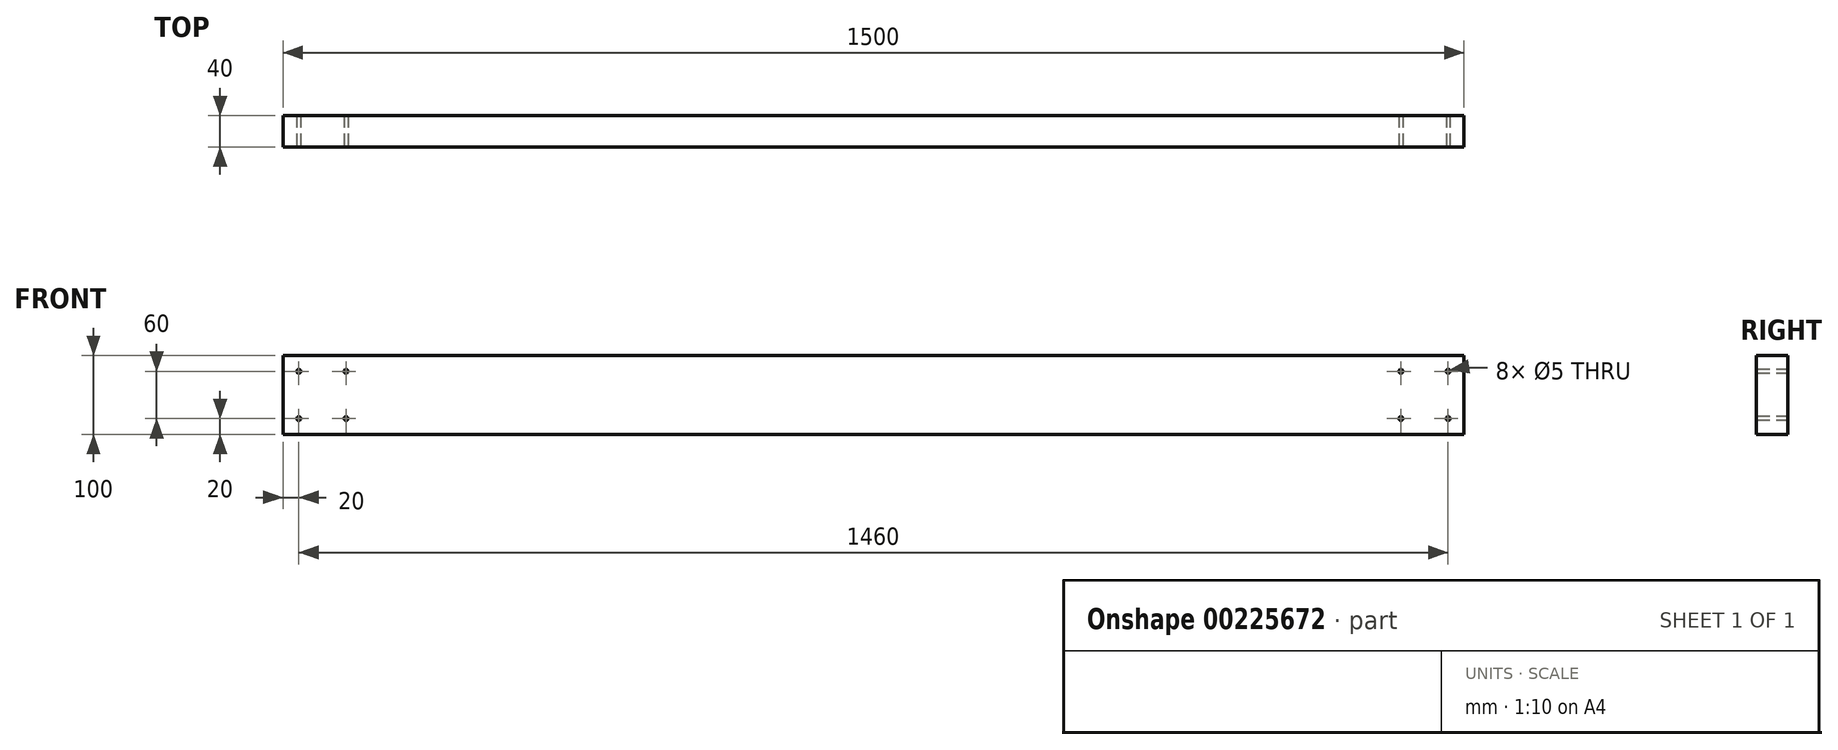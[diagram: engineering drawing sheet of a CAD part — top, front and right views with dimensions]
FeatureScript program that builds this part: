
annotation { "Feature Type Name" : "Feature", "Feature Type Description" : "" }
export const myFeature = defineFeature(function(context is Context, id is Id, definition is map)
    precondition{}
    {
        {
            var Q0;
            Q0=qCreatedBy(makeId("Front.planeOp"),FACE);
            var sketch = newSketch(context, id + "F0", { "sketchPlane" : qUnion([Q0])});
            skLineSegment(sketch, "E0.bottom", {"start": v(-750, 50) * mm, "end": v(750, 50) * mm});
            skLineSegment(sketch, "E0.top", {"start": v(-750, -50) * mm, "end": v(750, -50) * mm});
            skLineSegment(sketch, "E0.left", {"start": v(-750, 50) * mm, "end": v(-750, -50) * mm});
            skLineSegment(sketch, "E0.right", {"start": v(750, 50) * mm, "end": v(750, -50) * mm});
            skLineSegment(sketch, "E1", {"start": v(0, 50) * mm, "end": v(0, -50) * mm, "construction": true});
            skLineSegment(sketch, "E2", {"start": v(-750, 0) * mm, "end": v(750, 0) * mm, "construction": true});
            skSolve(sketch);
        }
        {
            var Q0;
            Q0=makeQuery(id+"F0.imprint","IMPRINT",FACE,{"disambiguationData":[TD([[makeQuery(id+"F0.imprint","IMPRINT",EDGE,{"derivedFrom":sQuery(id+"F0.wireOp",EDGE,"E0.bottom")}),-1.0]])]});
            extrude(context, id + "F1", {"entities" : qUnion([Q0]), "endBound" : BoundingType.SYMMETRIC, "depth" : 40 * mm});
        }
        {
            var Q0;
            Q0=makeQuery(id+"F1.opExtrude","CAP_FACE",FACE,{"disambiguationData":[OSD([sQuery(id+"F0.wireOp",EDGE,"E0.bottom"),sQuery(id+"F0.wireOp",EDGE,"E0.top"),sQuery(id+"F0.wireOp",EDGE,"E0.left"),sQuery(id+"F0.wireOp",EDGE,"E0.right")])],"isStart":false});
            var sketch = newSketch(context, id + "F2", { "sketchPlane" : qUnion([Q0])});
            skPoint(sketch, "E3", {"position": v(-730, 30) * mm});
            skPoint(sketch, "E4", {"position": v(-670, 30) * mm});
            skPoint(sketch, "E5", {"position": v(-730, -30) * mm});
            skPoint(sketch, "E6", {"position": v(-670, -30) * mm});
            skPoint(sketch, "E7", {"position": v(730, 30) * mm});
            skPoint(sketch, "E8", {"position": v(730, -30) * mm});
            skPoint(sketch, "E9", {"position": v(670, 30) * mm});
            skPoint(sketch, "E10", {"position": v(670, -30) * mm});
            skSolve(sketch);
        }
        {
            var Q0;
            Q0=sQuery(id+"F2.wireOp",VERTEX,"E3");
            var Q1;
            Q1=sQuery(id+"F2.wireOp",VERTEX,"E5");
            var Q2;
            Q2=sQuery(id+"F2.wireOp",VERTEX,"E4");
            var Q3;
            Q3=sQuery(id+"F2.wireOp",VERTEX,"E6");
            var Q4;
            Q4=sQuery(id+"F2.wireOp",VERTEX,"E9");
            var Q5;
            Q5=sQuery(id+"F2.wireOp",VERTEX,"E7");
            var Q6;
            Q6=sQuery(id+"F2.wireOp",VERTEX,"E10");
            var Q7;
            Q7=sQuery(id+"F2.wireOp",VERTEX,"E8");
            var Q8;
            Q8=makeQuery(id+"F1.opExtrude","SWEPT_BODY",BODY,{"disambiguationData":[OSD([sQuery(id+"F0.wireOp",EDGE,"E0.bottom"),sQuery(id+"F0.wireOp",EDGE,"E0.top"),sQuery(id+"F0.wireOp",EDGE,"E0.left"),sQuery(id+"F0.wireOp",EDGE,"E0.right")])]});
            hole(context, id + "F3", {"style" : HoleStyle.SIMPLE, "endStyle" : HoleEndStyle.THROUGH, "holeDiameter" : 5 * mm, "locations" : qUnion([Q0, Q1, Q2, Q3, Q4, Q5, Q6, Q7]), "scope" : qUnion([Q8]), "isTappedThrough" : true});
        }
    });
